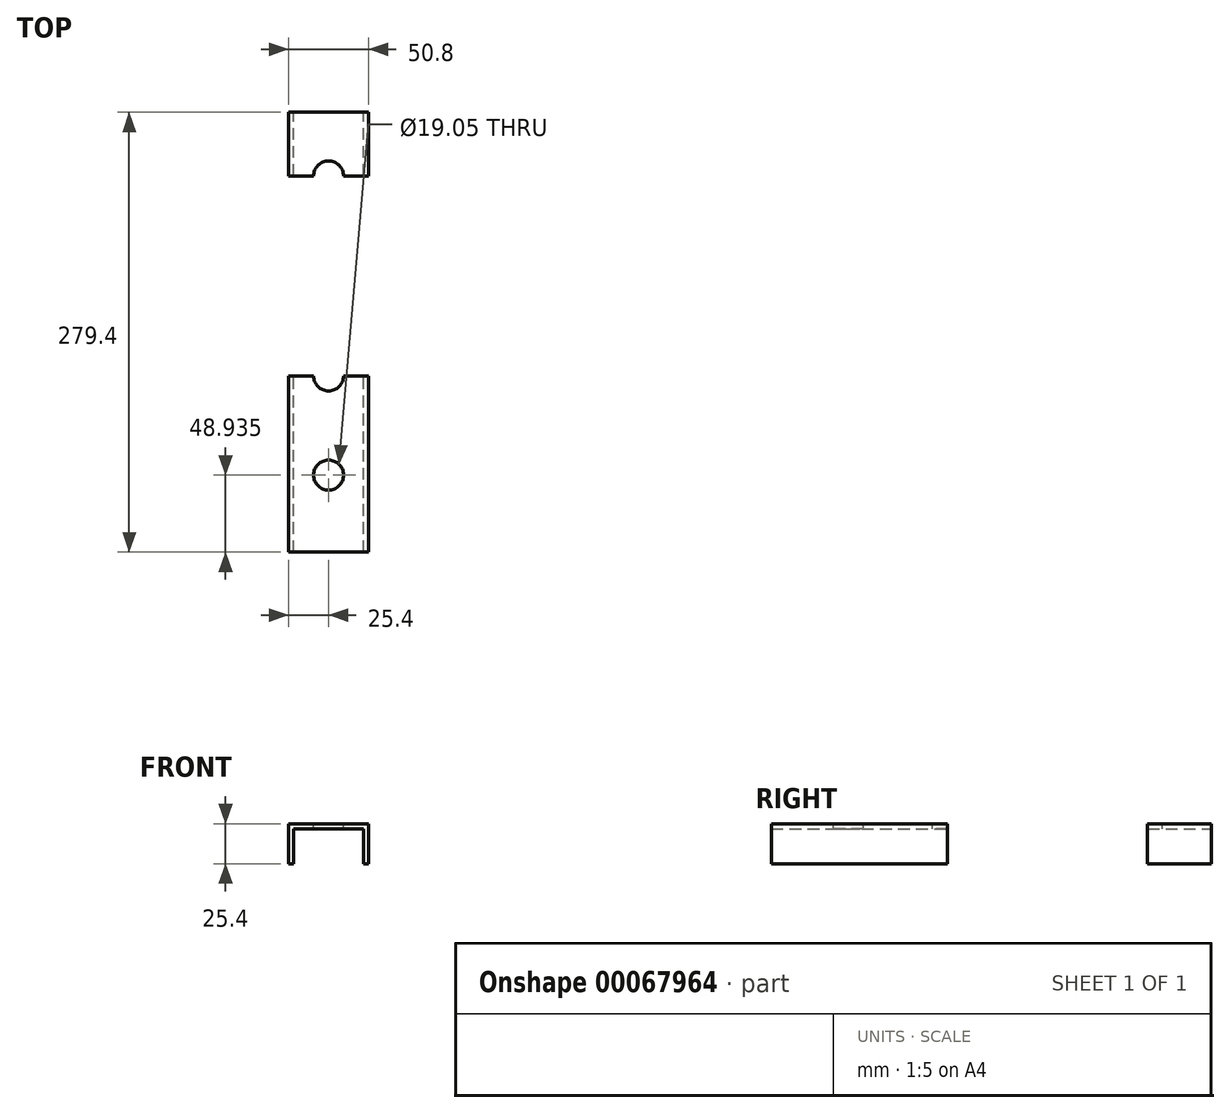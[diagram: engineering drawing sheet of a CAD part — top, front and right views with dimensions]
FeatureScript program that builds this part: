
annotation { "Feature Type Name" : "Feature", "Feature Type Description" : "" }
export const myFeature = defineFeature(function(context is Context, id is Id, definition is map)
    precondition{}
    {
        {
            var Q0;
            Q0=qCreatedBy(makeId("Front.planeOp"),FACE);
            var sketch = newSketch(context, id + "F0", { "sketchPlane" : qUnion([Q0])});
            skLineSegment(sketch, "E0.rect.bottom", {"start": v(25.4, 12.7) * mm, "end": v(-25.4, 12.7) * mm});
            skLineSegment(sketch, "E0.rect.left", {"start": v(25.4, 12.7) * mm, "end": v(25.4, -12.7) * mm});
            skLineSegment(sketch, "E0.rect.right", {"start": v(-25.4, 12.7) * mm, "end": v(-25.4, -12.7) * mm});
            skPoint(sketch, "E0.rect.middle", {"position": v(0, 0) * mm});
            skLineSegment(sketch, "E1", {"start": v(-25.4, -12.7) * mm, "end": v(-22.23, -12.7) * mm});
            skLineSegment(sketch, "E2", {"start": v(25.4, -12.7) * mm, "end": v(22.23, -12.7) * mm});
            skLineSegment(sketch, "E3", {"start": v(22.23, -12.7) * mm, "end": v(22.23, 9.53) * mm});
            skLineSegment(sketch, "E4", {"start": v(-22.23, -12.7) * mm, "end": v(-22.23, 9.53) * mm});
            skLineSegment(sketch, "E5", {"start": v(-22.23, 9.53) * mm, "end": v(22.23, 9.53) * mm});
            skSolve(sketch);
        }
        {
            var Q0;
            Q0=makeQuery(id+"F0.imprint","IMPRINT",FACE,{"disambiguationData":[TD([[makeQuery(id+"F0.imprint","IMPRINT",EDGE,{"derivedFrom":sQuery(id+"F0.wireOp",EDGE,"E0.rect.bottom")}),1.0]])]});
            extrude(context, id + "F1", {"entities" : qUnion([Q0]), "depth" : 279.4 * mm});
        }
        {
            var Q0;
            Q0=makeQuery(id+"F1.opExtrude","SWEPT_FACE",FACE,{"disambiguationData":[OSD([sQuery(id+"F0.wireOp",EDGE,"E0.rect.bottom")])]});
            var sketch = newSketch(context, id + "F2", { "sketchPlane" : qUnion([Q0])});
            skLineSegment(sketch, "E6", {"start": v(0, 0) * mm, "end": v(0, -279.4) * mm});
            skLineSegment(sketch, "E7", {"start": v(25.4, -40.43) * mm, "end": v(-25.4, -40.43) * mm});
            skCircle(sketch, "E8", {"center": v(0, -40.43) * mm, "radius": 9.53 * mm});
            skLineSegment(sketch, "E9", {"start": v(25.4, -103.93) * mm, "end": v(-25.4, -103.93) * mm});
            skLineSegment(sketch, "E10", {"start": v(25.4, -167.43) * mm, "end": v(-25.4, -167.43) * mm});
            skCircle(sketch, "E11", {"center": v(0, -103.93) * mm, "radius": 9.53 * mm});
            skCircle(sketch, "E12", {"center": v(0, -167.43) * mm, "radius": 9.53 * mm});
            skCircle(sketch, "E13", {"center": v(0, -230.46) * mm, "radius": 9.53 * mm});
            skLineSegment(sketch, "E14", {"start": v(25.4, -103.93) * mm, "end": v(25.4, -167.43) * mm});
            skLineSegment(sketch, "E15", {"start": v(25.4, -40.43) * mm, "end": v(25.4, -103.93) * mm});
            skLineSegment(sketch, "E16", {"start": v(-25.4, -230.46) * mm, "end": v(25.4, -230.46) * mm});
            skLineSegment(sketch, "E17", {"start": v(0, -230.46) * mm, "end": v(0, -265.8) * mm});
            skSolve(sketch);
        }
        {
            var Q0;
            {var subQ0=sQuery(id+"F2.wireOp",EDGE,"E8");var subQ1=sQuery(id+"F2.wireOp",EDGE,"E6");var subQ2=makeQuery(id+"F2.imprint","INTERSECT",VERTEX,{"disambiguationData":[OD(0.0)],"derivedFrom":[subQ1,subQ0]});Q0=makeQuery(id+"F2.imprint","IMPRINT",FACE,{"disambiguationData":[TD([[makeQuery(id+"F2.imprint","IMPRINT",EDGE,{"disambiguationData":[TD([[subQ2,-1.0]])],"derivedFrom":subQ1}),1.0]])]});}
            var Q1;
            {var subQ0=sQuery(id+"F2.wireOp",EDGE,"E8");var subQ1=sQuery(id+"F2.wireOp",EDGE,"E6");var subQ2=makeQuery(id+"F2.imprint","INTERSECT",VERTEX,{"disambiguationData":[OD(0.0)],"derivedFrom":[subQ1,subQ0]});Q1=makeQuery(id+"F2.imprint","IMPRINT",FACE,{"disambiguationData":[TD([[makeQuery(id+"F2.imprint","IMPRINT",EDGE,{"disambiguationData":[TD([[subQ2,-1.0]])],"derivedFrom":subQ1}),-1.0]])]});}
            var Q2;
            {var subQ0=sQuery(id+"F2.wireOp",EDGE,"E7");var subQ1=sQuery(id+"F2.wireOp",EDGE,"E6");var subQ2=makeQuery(id+"F2.imprint","INTERSECT",VERTEX,{"derivedFrom":[subQ1,subQ0]});Q2=makeQuery(id+"F2.imprint","IMPRINT",FACE,{"disambiguationData":[TD([[makeQuery(id+"F2.imprint","IMPRINT",EDGE,{"disambiguationData":[TD([[subQ2,-1.0]])],"derivedFrom":subQ1}),-1.0]])]});}
            var Q3;
            {var subQ0=sQuery(id+"F2.wireOp",EDGE,"E11");var subQ1=sQuery(id+"F2.wireOp",EDGE,"E6");var subQ2=makeQuery(id+"F2.imprint","INTERSECT",VERTEX,{"disambiguationData":[OD(0.0)],"derivedFrom":[subQ1,subQ0]});Q3=makeQuery(id+"F2.imprint","IMPRINT",FACE,{"disambiguationData":[TD([[makeQuery(id+"F2.imprint","IMPRINT",EDGE,{"disambiguationData":[TD([[subQ2,-1.0]])],"derivedFrom":subQ1}),1.0]])]});}
            var Q4;
            {var subQ0=sQuery(id+"F2.wireOp",EDGE,"E11");var subQ1=sQuery(id+"F2.wireOp",EDGE,"E6");var subQ2=makeQuery(id+"F2.imprint","INTERSECT",VERTEX,{"disambiguationData":[OD(0.0)],"derivedFrom":[subQ1,subQ0]});Q4=makeQuery(id+"F2.imprint","IMPRINT",FACE,{"disambiguationData":[TD([[makeQuery(id+"F2.imprint","IMPRINT",EDGE,{"disambiguationData":[TD([[subQ2,-1.0]])],"derivedFrom":subQ1}),-1.0]])]});}
            var Q5;
            {var subQ0=sQuery(id+"F2.wireOp",EDGE,"E9");var subQ1=sQuery(id+"F2.wireOp",EDGE,"E6");var subQ2=makeQuery(id+"F2.imprint","INTERSECT",VERTEX,{"derivedFrom":[subQ1,subQ0]});Q5=makeQuery(id+"F2.imprint","IMPRINT",FACE,{"disambiguationData":[TD([[makeQuery(id+"F2.imprint","IMPRINT",EDGE,{"disambiguationData":[TD([[subQ2,-1.0]])],"derivedFrom":subQ1}),1.0]])]});}
            var Q6;
            {var subQ0=sQuery(id+"F2.wireOp",EDGE,"E9");var subQ1=sQuery(id+"F2.wireOp",EDGE,"E6");var subQ2=makeQuery(id+"F2.imprint","INTERSECT",VERTEX,{"derivedFrom":[subQ1,subQ0]});Q6=makeQuery(id+"F2.imprint","IMPRINT",FACE,{"disambiguationData":[TD([[makeQuery(id+"F2.imprint","IMPRINT",EDGE,{"disambiguationData":[TD([[subQ2,-1.0]])],"derivedFrom":subQ1}),-1.0]])]});}
            var Q7;
            {var subQ0=sQuery(id+"F2.wireOp",EDGE,"E12");var subQ1=sQuery(id+"F2.wireOp",EDGE,"E6");var subQ2=makeQuery(id+"F2.imprint","INTERSECT",VERTEX,{"disambiguationData":[OD(0.0)],"derivedFrom":[subQ1,subQ0]});Q7=makeQuery(id+"F2.imprint","IMPRINT",FACE,{"disambiguationData":[TD([[makeQuery(id+"F2.imprint","IMPRINT",EDGE,{"disambiguationData":[TD([[subQ2,-1.0]])],"derivedFrom":subQ1}),1.0]])]});}
            var Q8;
            {var subQ0=sQuery(id+"F2.wireOp",EDGE,"E12");var subQ1=sQuery(id+"F2.wireOp",EDGE,"E6");var subQ2=makeQuery(id+"F2.imprint","INTERSECT",VERTEX,{"disambiguationData":[OD(0.0)],"derivedFrom":[subQ1,subQ0]});Q8=makeQuery(id+"F2.imprint","IMPRINT",FACE,{"disambiguationData":[TD([[makeQuery(id+"F2.imprint","IMPRINT",EDGE,{"disambiguationData":[TD([[subQ2,-1.0]])],"derivedFrom":subQ1}),-1.0]])]});}
            var Q9;
            {var subQ0=sQuery(id+"F2.wireOp",EDGE,"E10");var subQ1=sQuery(id+"F2.wireOp",EDGE,"E6");var subQ2=makeQuery(id+"F2.imprint","INTERSECT",VERTEX,{"derivedFrom":[subQ1,subQ0]});Q9=makeQuery(id+"F2.imprint","IMPRINT",FACE,{"disambiguationData":[TD([[makeQuery(id+"F2.imprint","IMPRINT",EDGE,{"disambiguationData":[TD([[subQ2,-1.0]])],"derivedFrom":subQ1}),1.0]])]});}
            var Q10;
            {var subQ0=sQuery(id+"F2.wireOp",EDGE,"E10");var subQ1=sQuery(id+"F2.wireOp",EDGE,"E6");var subQ2=makeQuery(id+"F2.imprint","INTERSECT",VERTEX,{"derivedFrom":[subQ1,subQ0]});Q10=makeQuery(id+"F2.imprint","IMPRINT",FACE,{"disambiguationData":[TD([[makeQuery(id+"F2.imprint","IMPRINT",EDGE,{"disambiguationData":[TD([[subQ2,-1.0]])],"derivedFrom":subQ1}),-1.0]])]});}
            var Q11;
            {var subQ0=sQuery(id+"F2.wireOp",EDGE,"E13");var subQ1=sQuery(id+"F2.wireOp",EDGE,"E6");var subQ2=makeQuery(id+"F2.imprint","INTERSECT",VERTEX,{"disambiguationData":[OD(0.0)],"derivedFrom":[subQ1,subQ0]});Q11=makeQuery(id+"F2.imprint","IMPRINT",FACE,{"disambiguationData":[TD([[makeQuery(id+"F2.imprint","IMPRINT",EDGE,{"disambiguationData":[TD([[subQ2,-1.0]])],"derivedFrom":subQ1}),1.0]])]});}
            var Q12;
            {var subQ0=sQuery(id+"F2.wireOp",EDGE,"E13");var subQ1=sQuery(id+"F2.wireOp",EDGE,"E6");var subQ2=makeQuery(id+"F2.imprint","INTERSECT",VERTEX,{"disambiguationData":[OD(0.0)],"derivedFrom":[subQ1,subQ0]});Q12=makeQuery(id+"F2.imprint","IMPRINT",FACE,{"disambiguationData":[TD([[makeQuery(id+"F2.imprint","IMPRINT",EDGE,{"disambiguationData":[TD([[subQ2,-1.0]])],"derivedFrom":subQ1}),-1.0]])]});}
            var Q13;
            {var subQ0=sQuery(id+"F2.wireOp",EDGE,"8fdee2cb-ed79-4f0d-a621-2c9df3bafdf6");var subQ1=sQuery(id+"F2.wireOp",EDGE,"E6");var subQ2=makeQuery(id+"F2.imprint","INTERSECT",VERTEX,{"derivedFrom":[subQ1,subQ0]});Q13=makeQuery(id+"F2.imprint","IMPRINT",FACE,{"disambiguationData":[TD([[makeQuery(id+"F2.imprint","IMPRINT",EDGE,{"disambiguationData":[TD([[subQ2,-1.0]])],"derivedFrom":subQ1}),1.0]])]});}
            var Q14;
            {var subQ0=sQuery(id+"F2.wireOp",EDGE,"8fdee2cb-ed79-4f0d-a621-2c9df3bafdf6");var subQ1=sQuery(id+"F2.wireOp",EDGE,"E6");var subQ2=makeQuery(id+"F2.imprint","INTERSECT",VERTEX,{"derivedFrom":[subQ1,subQ0]});Q14=makeQuery(id+"F2.imprint","IMPRINT",FACE,{"disambiguationData":[TD([[makeQuery(id+"F2.imprint","IMPRINT",EDGE,{"disambiguationData":[TD([[subQ2,-1.0]])],"derivedFrom":subQ1}),-1.0]])]});}
            var Q15;
            {var subQ0=sQuery(id+"F2.wireOp",EDGE,"E7");var subQ1=sQuery(id+"F2.wireOp",EDGE,"E6");var subQ2=makeQuery(id+"F2.imprint","INTERSECT",VERTEX,{"derivedFrom":[subQ1,subQ0]});Q15=makeQuery(id+"F2.imprint","IMPRINT",FACE,{"disambiguationData":[TD([[makeQuery(id+"F2.imprint","IMPRINT",EDGE,{"disambiguationData":[TD([[subQ2,-1.0]])],"derivedFrom":subQ1}),1.0]])]});}
            extrude(context, id + "F3", {"entities" : qUnion([Q0, Q1, Q2, Q3, Q4, Q5, Q6, Q7, Q8, Q9, Q10, Q11, Q12, Q13, Q14, Q15]), "operationType" : NewBodyOperationType.REMOVE, "endBound" : BoundingType.THROUGH_ALL, "oppositeDirection" : true, "depth" : 25.4 * mm});
        }
        {
            var Q0;
            Q0=makeQuery(id+"F1.opExtrude","SWEPT_FACE",FACE,{"disambiguationData":[OSD([sQuery(id+"F0.wireOp",EDGE,"E0.rect.bottom")])]});
            var sketch = newSketch(context, id + "F4", { "sketchPlane" : qUnion([Q0])});
            skLineSegment(sketch, "E18", {"start": v(0, -220.94) * mm, "end": v(0, -230.46) * mm});
            skSolve(sketch);
        }
        {
            var Q0;
            Q0=sQuery(id+"F4.wireOp",VERTEX,"E18.end");
            var Q1;
            Q1=makeQuery(id+"F1.opExtrude","SWEPT_BODY",BODY,{"disambiguationData":[OSD([sQuery(id+"F0.wireOp",EDGE,"E0.rect.bottom"),sQuery(id+"F0.wireOp",EDGE,"E0.rect.left"),sQuery(id+"F0.wireOp",EDGE,"E0.rect.right"),sQuery(id+"F0.wireOp",EDGE,"E1"),sQuery(id+"F0.wireOp",EDGE,"E2"),sQuery(id+"F0.wireOp",EDGE,"E3"),sQuery(id+"F0.wireOp",EDGE,"E4"),sQuery(id+"F0.wireOp",EDGE,"E5")])]});
            hole(context, id + "F5", {"style" : HoleStyle.SIMPLE, "holeDiameter" : 19.05 * mm, "endStyle" : HoleEndStyle.THROUGH, "locations" : qUnion([Q0]), "scope" : qUnion([Q1])});
        }
    });
